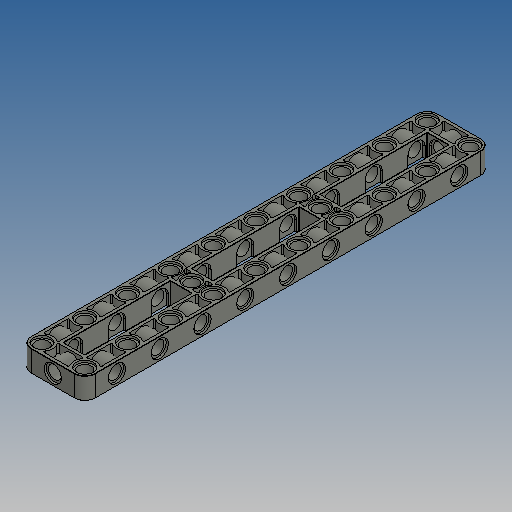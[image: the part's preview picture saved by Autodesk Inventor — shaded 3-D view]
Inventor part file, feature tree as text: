
AUTODESK INVENTOR PART (.ipt)
format: ipt  version: 2025 (Build 290162010, 162A)  size: 1,363,968 bytes
history: native  units: mm
features: extrude x17, sketch x14, mirror x3, fillet x1, projected_geometry x1
ambient origin geometry x8: Origin, YZ Plane, XZ Plane, XY Plane, X Axis, Y Axis, Z Axis, Center Point
bodies: Solid1 (feature_tree)
feature tree (36):
  extrude  "Extrusion1"  Depth=0.8mm TaperAngle=0.0deg
  sketch  "Sketch6"  dims[d49=6.4mm d50=4.8mm]
  extrude  "Extrusion7"  Depth=48.0mm
  extrude  "Extrusion8"  Depth=6.4mm
  extrude  "Extrusion19"  Depth=0.4mm
  mirror  "Mirror5"
  sketch  "Sketch7"  dims[d51=16.0mm d60=0.4mm d61=0.1mm]
  extrude  "Extrusion9"  Depth=7.2mm
  extrude  "Extrusion10"  Depth=10.0mm TaperAngle=0.0deg
  extrude  "Extrusion11"  Depth=6.4mm
  extrude  "Extrusion18"  Depth=6.4mm
  extrude  "Extrusion20"  TaperAngle=0.0deg  [1 undecoded]
  extrude  "Extrusion27"  Depth=1.6mm
  extrude  "Extrusion28"  Depth=16.0mm
  extrude  "Extrusion21"  Depth=56.0mm
  sketch  "Skizze18"  dims[d112=3.1mm d113=0.0mm d114=16.0mm]
  extrude  "Extrusion22"  Depth=16.0mm
  extrude  "Extrusion23"  Depth=8.0mm
  fillet  "Fillet2"  Radius=0.8mm
  sketch  "Sketch12"  dims[d70=4.8mm d71=10.0mm d72=0.0mm]
  extrude  "Extrusion24"  Depth=1.6mm
  extrude  "Extrusion25"  Depth=1.172mm
  extrude  "Extrusion26"  Depth=10.0mm TaperAngle=0.0deg
  mirror  "Mirror4"
  mirror  "Mirror3"
  sketch  "Sketch1"  dims[d14=8.0mm d15=0.0mm d41=0.8mm d42=0.0mm]
  projected_geometry  "Projected Loop4"
  sketch  "Skizze - Rechteckige Anordnung1"  dims[d43=3.1mm d44=0.0mm d48=48.0mm]
  sketch  "Sketch8"  dims[d62=30.0mm d64=16.0mm d65=10.0mm d67=10.0mm d69=7.2mm]
  sketch  "Sketch14"  dims[d73=10.0mm d74=0.0mm d75=6.4mm]
  sketch  "Sketch15"  dims[d76=0.8mm d77=0.0mm d106=6.4mm]
  sketch  "Skizze16"  dims[d107=0.8mm d108=0.0mm]
  sketch  "Skizze17"  dims[d109=45.0deg d111=1.6mm]
  sketch  "Skizze19"  dims[d116=45.0deg d117=56.0mm]
  sketch  "Skizze20"  dims[d118=8.0mm d119=16.0mm]
  sketch  "Skizze21"  dims[d120=16.0mm d121=8.0mm d122=0.8mm d123=0.0mm d124=1.6mm d125=1.172mm d126=10.0mm d127=0.0mm d128=1.172mm d129=0.4mm d131=0.0mm d132=0.0mm d133=6.4mm d134=8.0mm d135=3.2mm d136=0.8mm d137=0.0mm d138=7.2mm d139=4.8mm d140=6.4mm d141=0.0mm d142=10.0mm d143=0.0mm d144=0.8mm d145=0.0mm d146=10.0mm d147=0.0mm d148=10.0mm d149=0.0mm d150=1.172mm d151=1.172mm d152=0.6mm d153=0.4mm]
note: 1 required parameter value undecoded (feature->parameter linkage not recoverable at this tier; creation-order binding heuristic only, values carry confidence <= 0.55)
